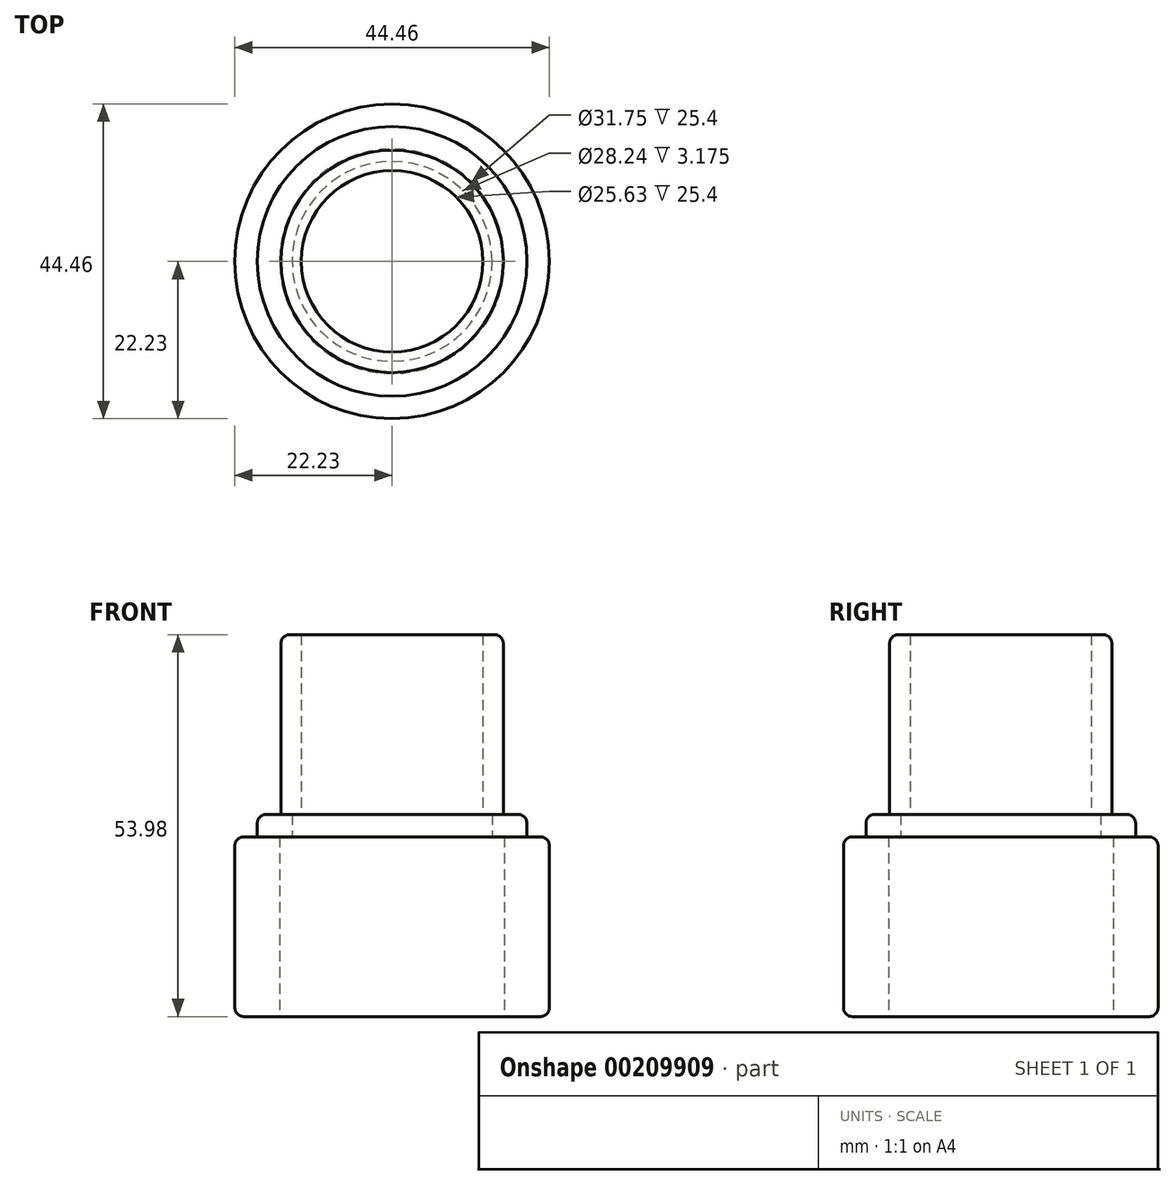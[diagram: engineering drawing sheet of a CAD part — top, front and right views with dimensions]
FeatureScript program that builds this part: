
annotation { "Feature Type Name" : "Feature", "Feature Type Description" : "" }
export const myFeature = defineFeature(function(context is Context, id is Id, definition is map)
    precondition{}
    {
        {
            var Q0;
            Q0=qCreatedBy(makeId("Top.planeOp"),FACE);
            var sketch = newSketch(context, id + "F0", { "sketchPlane" : qUnion([Q0])});
            skCircle(sketch, "E0", {"center": v(0, 0) * mm, "radius": 15.88 * mm});
            skCircle(sketch, "E1.0", {"center": v(0, 0) * mm, "radius": 22.23 * mm});
            skSolve(sketch);
        }
        {
            var Q0;
            Q0 = qSketchRegion(id + "F0", true);
            extrude(context, id + "F1", {"entities" : qUnion([Q0]), "depth" : 25.4 * mm});
        }
        {
            var Q0;
            Q0=makeQuery(id+"F1.opExtrude","CAP_FACE",FACE,{"disambiguationData":[OSD([sQuery(id+"F0.wireOp",EDGE,"E0"),sQuery(id+"F0.wireOp",EDGE,"E1.0")])],"isStart":false});
            var sketch = newSketch(context, id + "F2", { "sketchPlane" : qUnion([Q0])});
            skCircle(sketch, "E2", {"center": v(0, 0) * mm, "radius": 19.05 * mm});
            skCircle(sketch, "E3", {"center": v(0, 0) * mm, "radius": 14.12 * mm});
            skSolve(sketch);
        }
        {
            var Q0;
            Q0 = qSketchRegion(id + "F2", true);
            extrude(context, id + "F3", {"entities" : qUnion([Q0]), "operationType" : NewBodyOperationType.ADD, "depth" : 3.17 * mm});
        }
        {
            var Q0;
            Q0=makeQuery(id+"F3.opExtrude","CAP_FACE",FACE,{"disambiguationData":[OSD([sQuery(id+"F2.wireOp",EDGE,"E2"),sQuery(id+"F2.wireOp",EDGE,"E3")])],"isStart":false});
            var sketch = newSketch(context, id + "F4", { "sketchPlane" : qUnion([Q0])});
            skCircle(sketch, "E4", {"center": v(0, 0) * mm, "radius": 15.7 * mm});
            skCircle(sketch, "E5.0", {"center": v(0, 0) * mm, "radius": 12.81 * mm});
            skSolve(sketch);
        }
        {
            var Q0;
            Q0 = qSketchRegion(id + "F4", true);
            extrude(context, id + "F5", {"entities" : qUnion([Q0]), "operationType" : NewBodyOperationType.ADD, "depth" : 25.4 * mm});
        }
        {
            var Q0;
            Q0=makeQuery(id+"F5.opExtrude","CAP_EDGE",EDGE,{"disambiguationData":[OSD([sQuery(id+"F4.wireOp",EDGE,"E4")])],"isStart":false});
            var Q1;
            Q1=makeQuery(id+"F3.opExtrude","CAP_EDGE",EDGE,{"disambiguationData":[OSD([sQuery(id+"F2.wireOp",EDGE,"E2")])],"isStart":false});
            var Q2;
            Q2=makeQuery(id+"F1.opExtrude","CAP_EDGE",EDGE,{"disambiguationData":[OSD([sQuery(id+"F0.wireOp",EDGE,"E1.0")])],"isStart":false});
            var Q3;
            Q3=makeQuery(id+"F5.opExtrude","CAP_EDGE",EDGE,{"disambiguationData":[OSD([sQuery(id+"F4.wireOp",EDGE,"E4")])],"isStart":true});
            var Q4;
            Q4=makeQuery(id+"F1.opExtrude","CAP_EDGE",EDGE,{"disambiguationData":[OSD([sQuery(id+"F0.wireOp",EDGE,"E1.0")])],"isStart":true});
            var Q5;
            Q5=makeQuery(id+"F3.opExtrude","CAP_EDGE",EDGE,{"disambiguationData":[OSD([sQuery(id+"F2.wireOp",EDGE,"E2")])],"isStart":true});
            fillet(context, id + "F6", {"entities" : qUnion([Q0, Q1, Q2, Q3, Q4, Q5]), "radius" : 1.27 * mm, "tangentPropagation" : true, "allowEdgeOverflow" : false});
        }
    });
